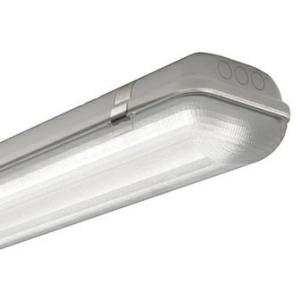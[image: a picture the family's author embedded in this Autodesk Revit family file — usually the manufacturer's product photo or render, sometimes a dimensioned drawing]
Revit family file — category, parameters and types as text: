
# Revit family: 3f_filippi_-_3f_linda_3f_filippi_-_58616_-_3f_linda_led_2x30w_l1570
name_source: partatom
category: Lighting Fixtures
units: mm (PartAtom-declared; Revit-internal decimal feet)

## family parameters
Cut with Voids When Loaded = No
Host = Face
Light Source = No
Part Type = Normal
Room Calculation Point = No
Round Connector Dimension = Use Diameter
Shared = No

## types (1)
- 3F Filippi - 3F Linda (1 x LED, 9715 lm, 66 W, 4000 K)
    Apparent Load = 66 VA
    Approval mark = CE
    CIE Flux Codes = 46 76 93 97 100
    Color Rendering = 80
    Color Temperature = 4000 K
    Control Gear = Electronic ballast
    Default Elevation = 1800 mm
    Description = ILLUMINOTECHNICAL
Luminous efficiency 100% (DLOR 97%, ULOR 3%).
Initial luminous flux of the luminaire 9715 lm.
Controlled symmetric distribution.
Installation Interdistance Transv.D = 1.52 x hu - Long.D = 1.17 x hu.
Tabular UGR (CIE 117 - 4H-8H; S=0.25H; 70/50/20): RUG 24.3 - 23.5.
Beam angle: 94° - 78°.
Luminous efficacy 147 lm/W.
Lifetime (L93/B10): 30000 h. (tq+25°C)
Lifetime (L90/B10): 50000 h. (tq+25°C)
Lifetime (L85/B10): 80000 h. (tq+25°C)
Lifetime (L80/B10): 100000 h. (tq+25°C)
Lifetime (L85/B10): 50000 h. (tq+35°C)
Sudden decreased luminous flux after 50000 hours: 0% (C0).
Photobiological safety in compliance with IEC/TR 62778: RG0 risk exempt, (IEC 62471).
In compliance with IEC/EN 62722-2-1 - IEC/EN 62717 standards.

SOURCE
2 linear LED modules 30W/840.
Energy efficiency class (UE 2019/2020 - UE 2019/2015): D.
CIE 13.3 Colour rendering index: CRI >80 (R9 <50%).
IES TM-30 Fidelity Index: Rf = 84 Rg = 95.
CCT nominal colour temperature 4000 K.
Colour initial tolerance (MacAdam): SDCM 3.

MECHANICAL
Self-extinguishing V2 polycarbonate housing, injection moulded, RAL 7035 grey.
Ecologic anti-aging injected sealing gasket.
Diffuser in self-extinguishing V2 polycarbonate, photo-engraved interior, UV stabilised, injection moulded with smooth outer surface, tamper-proof opening.
Gear-holder reflector in hot-dip galvanised steel, painted with white polyester base.
Snug fit safety snap-lock clips for diffuser mounting in stainless steel, screwdriver opening.
Fixing brackets in stainless steel.
Possibility for technicians to access the interior of the luminaire.
Luminaire with limited surface temperature. - D - (EN 60598-2-24)
Dimensions: 1570x160 mm, height 100 mm. Weight 3.348 kg.
IP66 protection degree.
Mechanical strength to impacts IK10 (20 joule).
Glow-wire test resistance 850°C.

ELECTRICAL
Halogen Free electronic wiring 230V-50/60Hz, power factor 0.97, THD <25%, constant output current, SELV, class I, 1 driver.
Power of the luminaire 66 W.
ENEC - CE.
SAFE FLICKER: PstLM=<1 and SVM=<0.4 (IEC TR 61547-1 and IEC TR 63158), to ensure a more comfortable and safe light.
Luminaire compliant with EN 60598-2-22 for power supply from a centralised emergency system CPSS (Central Power Supply System), not incorporated in the luminaire - high risk areas excluded. The default power and flux are 100% in AC and 100% in DC.
Ambient temperature from -20°C to +35°C.
Temperature class T6 max 85°C.
Relative humidity UR: <85%.

INSTALLATION
Ceiling / Suspended / Wall.
All accessories dedicated to this product are available on the Catalog and on our website www.3F-Filippi.com.

APPLICATIONS
Suitable product for food production plants (HACCP), IFS (Food Version 6), BRC (GSFS Food Version 7).
Dry, dusty indoor environments, subject to occasional water splashes.
Virtually shatterproof polycarbonate compatibly with the fumes / atmospheres that compromise the elasticity of plastic materials.
Not suitable for installation on surfaces subject to important vibrations, exposed to weather conditions, on ropes or poles.
Suitable for illumination of public car parks and parking grounds referred to DIN 67528:2018-04.

WARNING
Fixture not suitable for cold stores with an ambient temperature <0°C and/or relative humidity >85%.
Luminaire designed for disposal/recycling at end-of-life.
Replaceable (LED only) light source by a professional. Replaceable control gear by a professional.
    Height = 100 mm  [stored 0.328084 ft]
    Lamp = 1 x LED
    Lamp Light Flux = 9715 lm
    Lamp Power = 66 W
    Lamp count = 1
    Length = 1570 mm
    Lifetime = 50000 h
    Luminous efficacy = 147 lm/W
    Manufacturer = 3F Filippi
    ModVariant = No
    Model = 3F Filippi - 58616 - 3F Linda LED 2x30W L1570
    Mounting Place = Ceiling
    Mounting Type = Pendant
    Number of Poles = 1
    OnlyDefault = Yes
    Power Factor = 1
    Product Name = 3F Filippi - 3F Linda
    Product group = pendant luminaire
    ProductGroupID = 9
    Protection Class = Protection class I
    Protection Degree = IP 66
    RLX_Detail_Level = 1
    RLX_Emergency_Light_Flux = 0 lm
    RLX_Emergency_Type = 0
    RLX_Emergency_Type_DB = No
    RlxData = <blob elided: 71349 chars, md5=252a83bf>
    Socket = socket
    Standby Power = 0 W
    System Light Flux = 9715 lm
    System Power = 66 W
    Type Comments = Product without accessories
    Type Image = 3ffilippi_3f_linda_led_2x.jpg
    URL = http://relux.com
    VarID = ---
    Voltage = 0 V
    Weight = 0.00 kg
    Width = 160 mm

note: [stored X ft] marks values corroborated as IEEE doubles in the binary element streams (Revit-internal decimal feet)

## geometry (parser evidence)
native form markers: Blend x4, Sweep x10
no freeform markers — native parametric forms only
